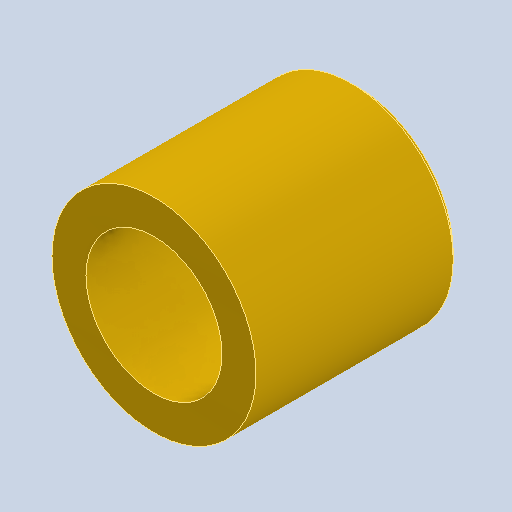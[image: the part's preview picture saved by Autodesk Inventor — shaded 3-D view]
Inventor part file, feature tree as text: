
AUTODESK INVENTOR PART (.ipt)
format: ipt  version: 2022 (Build 260153000, 153)  size: 106,496 bytes
history: native  units: in
note: dims shown in document units (in); Inventor stores cm internally (conversion verified against a paired STEP export)
features: other x3, sketch x1
ambient origin geometry x8: Origin, YZ Plane, XZ Plane, XY Plane, X Axis, Y Axis, Z Axis, Center Point
bodies: Solid1 (feature_tree)
feature tree (4):
  other  "bush.ipt"
  other  "Solid1::bush.ipt"
  other  "TaggingFeature1"
  sketch  "Sketch1"  dims[d0=0.3937in]
